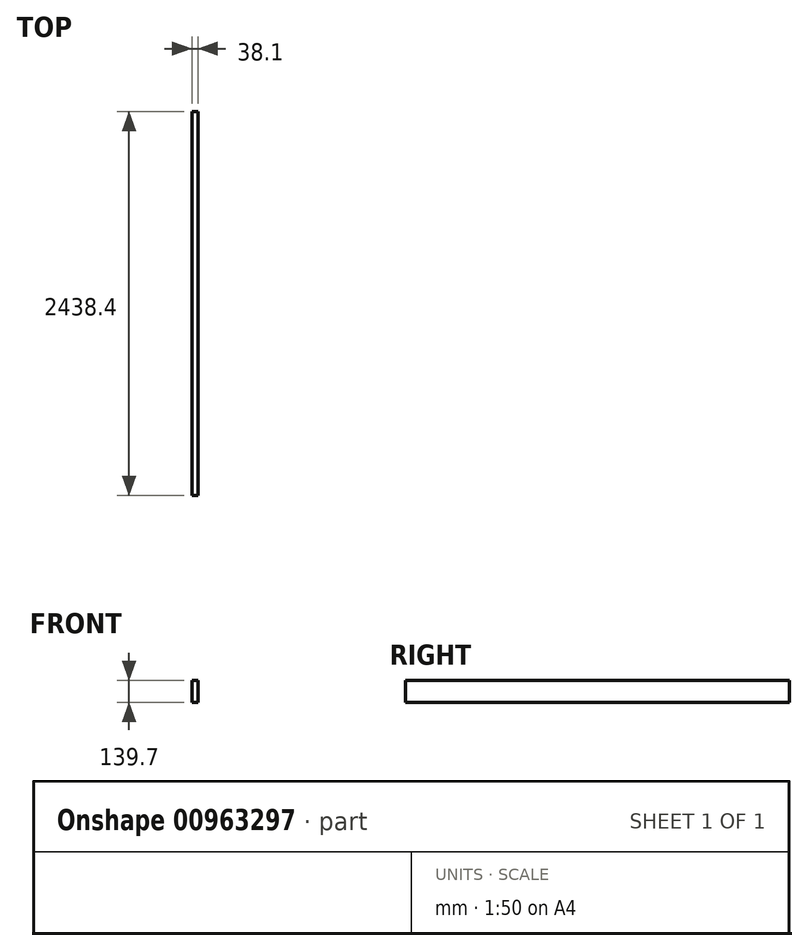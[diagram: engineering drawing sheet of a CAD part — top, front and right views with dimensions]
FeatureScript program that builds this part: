
annotation { "Feature Type Name" : "Feature", "Feature Type Description" : "" }
export const myFeature = defineFeature(function(context is Context, id is Id, definition is map)
    precondition{}
    {
        {
            var Q0;
            Q0=qCreatedBy(makeId("Front.planeOp"),FACE);
            var sketch = newSketch(context, id + "F0", { "sketchPlane" : qUnion([Q0])});
            skLineSegment(sketch, "E0.bottom", {"start": v(0, 0) * mm, "end": v(38.1, 0) * mm});
            skLineSegment(sketch, "E0.top", {"start": v(0, 139.7) * mm, "end": v(38.1, 139.7) * mm});
            skLineSegment(sketch, "E0.left", {"start": v(0, 0) * mm, "end": v(0, 139.7) * mm});
            skLineSegment(sketch, "E0.right", {"start": v(38.1, 0) * mm, "end": v(38.1, 139.7) * mm});
            skSolve(sketch);
        }
        {
            var Q0;
            Q0=makeQuery(id+"F0.imprint","IMPRINT",FACE,{"disambiguationData":[TD([[makeQuery(id+"F0.imprint","IMPRINT",EDGE,{"derivedFrom":sQuery(id+"F0.wireOp",EDGE,"E0.bottom")}),1.0]])]});
            extrude(context, id + "F1", {"entities" : qUnion([Q0]), "offsetDistance" : 25.4 * mm, "depth" : 2438.4 * mm});
        }
    });
